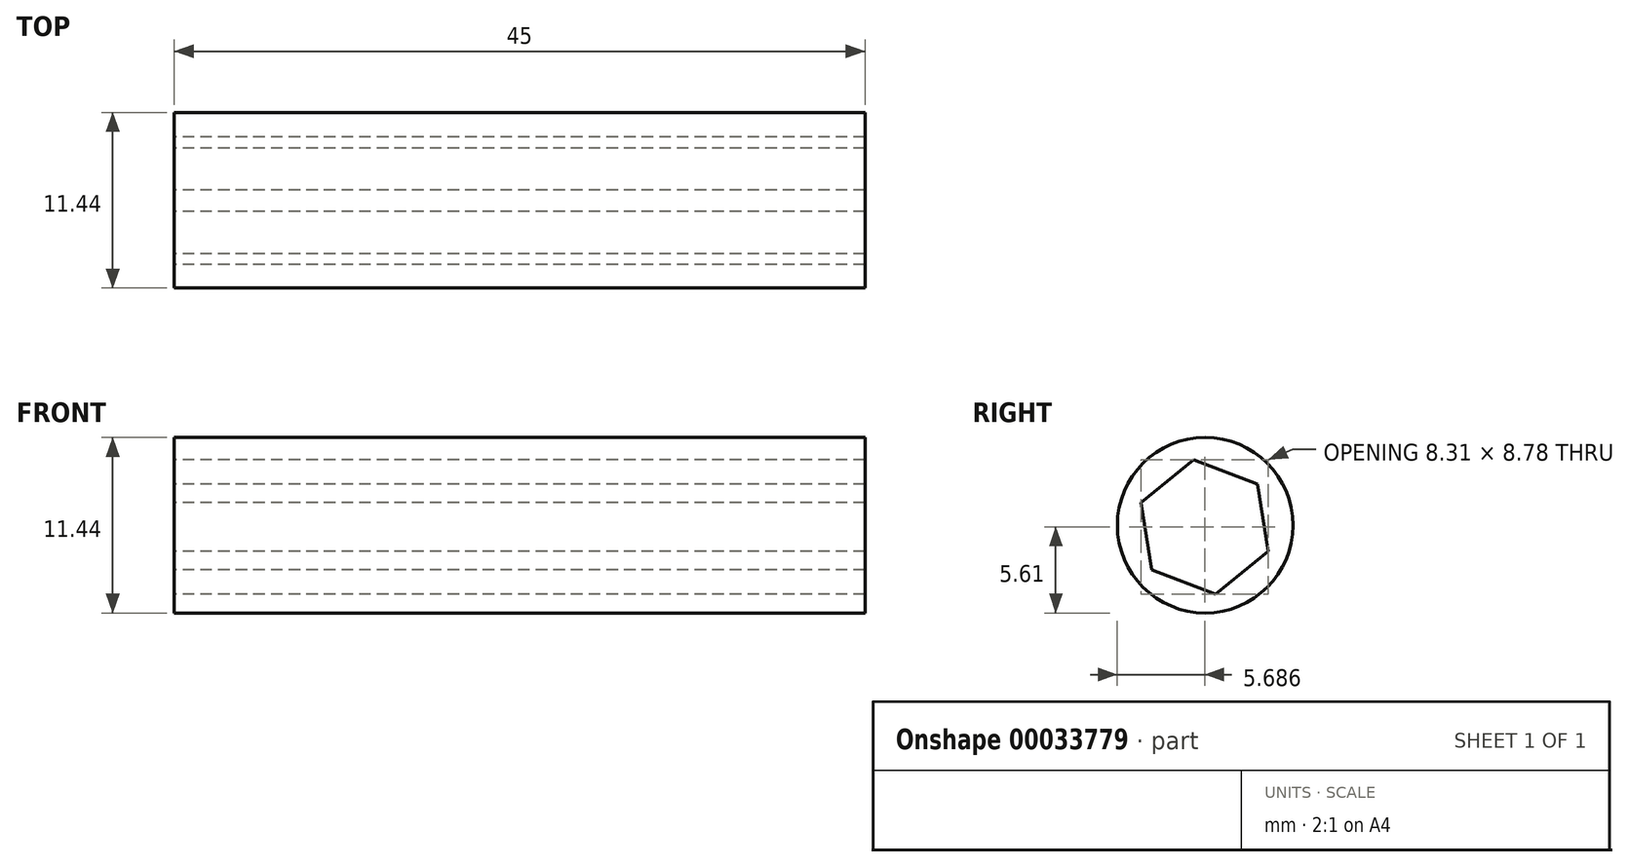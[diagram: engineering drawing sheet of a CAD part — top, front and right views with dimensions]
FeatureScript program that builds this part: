
annotation { "Feature Type Name" : "Feature", "Feature Type Description" : "" }
export const myFeature = defineFeature(function(context is Context, id is Id, definition is map)
    precondition{}
    {
        {
            var Q0;
            Q0=qCreatedBy(makeId("Right.planeOp"),FACE);
            var sketch = newSketch(context, id + "F0", { "sketchPlane" : qUnion([Q0])});
            skCircle(sketch, "E0", {"center": v(-26.87, 8.05) * mm, "radius": 5.72 * mm});
            skSolve(sketch);
        }
        {
            var Q0;
            Q0=makeQuery(id+"F0.imprint","IMPRINT",FACE,{"disambiguationData":[TD([[makeQuery(id+"F0.imprint","IMPRINT",EDGE,{"derivedFrom":sQuery(id+"F0.wireOp",EDGE,"E0")}),1.0]])]});
            var Q1;
            Q1=sQuery(id+"F0.wireOp",EDGE,"E0");
            extrude(context, id + "F1", {"entities" : qUnion([Q0]), "surfaceEntities" : qUnion([Q1]), "depth" : 45 * mm});
        }
        {
            var Q0;
            Q0=qCreatedBy(makeId("Right.planeOp"),FACE);
            var sketch = newSketch(context, id + "F2", { "sketchPlane" : qUnion([Q0])});
            skCircle(sketch, "E1.cCircle", {"center": v(-26.9, 7.94) * mm, "radius": 3.85 * mm, "construction": true});
            skLineSegment(sketch, "E1.0", {"start": v(-22.75, 6.35) * mm, "end": v(-26.2, 3.55) * mm});
            skLineSegment(sketch, "E1.1", {"start": v(-26.2, 3.55) * mm, "end": v(-30.36, 5.14) * mm});
            skLineSegment(sketch, "E1.2", {"start": v(-30.36, 5.14) * mm, "end": v(-31.06, 9.53) * mm});
            skLineSegment(sketch, "E1.3", {"start": v(-31.06, 9.53) * mm, "end": v(-27.6, 12.33) * mm});
            skLineSegment(sketch, "E1.4", {"start": v(-27.6, 12.33) * mm, "end": v(-23.45, 10.74) * mm});
            skLineSegment(sketch, "E1.5", {"start": v(-23.45, 10.74) * mm, "end": v(-22.75, 6.35) * mm});
            skPoint(sketch, "E1.0.midPoint", {"position": v(-24.48, 4.95) * mm});
            skSolve(sketch);
        }
        {
            var Q0;
            Q0 = qSketchRegion(id + "F2", true);
            extrude(context, id + "F3", {"entities" : qUnion([Q0]), "operationType" : NewBodyOperationType.REMOVE, "endBound" : BoundingType.THROUGH_ALL, "depth" : 45 * mm});
        }
    });
